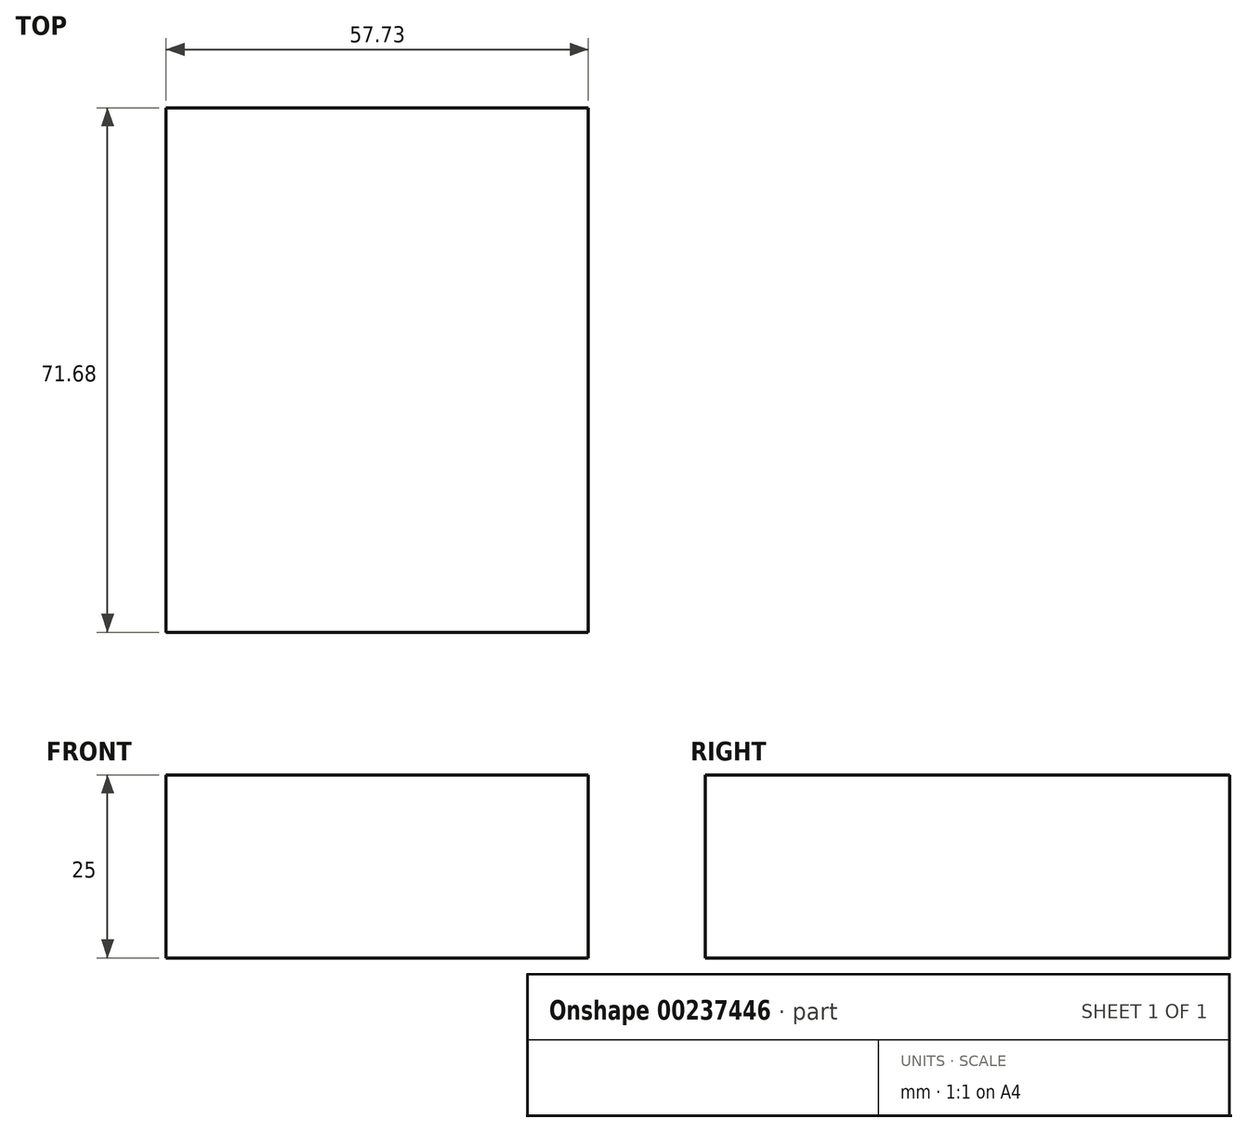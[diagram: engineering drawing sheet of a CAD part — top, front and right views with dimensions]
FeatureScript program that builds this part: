
annotation { "Feature Type Name" : "Feature", "Feature Type Description" : "" }
export const myFeature = defineFeature(function(context is Context, id is Id, definition is map)
    precondition{}
    {
        {
            var Q0;
            Q0=qCreatedBy(makeId("Top.planeOp"),FACE);
            var sketch = newSketch(context, id + "F0", { "sketchPlane" : qUnion([Q0])});
            skLineSegment(sketch, "E0.bottom", {"start": v(-76.87, -35.84) * mm, "end": v(-134.6, -35.84) * mm});
            skLineSegment(sketch, "E0.top", {"start": v(-76.87, 35.84) * mm, "end": v(-134.6, 35.84) * mm});
            skLineSegment(sketch, "E0.left", {"start": v(-76.87, -35.84) * mm, "end": v(-76.87, 35.84) * mm});
            skLineSegment(sketch, "E0.right", {"start": v(-134.6, -35.84) * mm, "end": v(-134.6, 35.84) * mm});
            skPoint(sketch, "E0.middle", {"position": v(-105.73, 0) * mm});
            skSolve(sketch);
        }
        {
            var Q0;
            Q0=makeQuery(id+"F0.imprint","IMPRINT",FACE,{"disambiguationData":[TD([[makeQuery(id+"F0.imprint","IMPRINT",EDGE,{"derivedFrom":sQuery(id+"F0.wireOp",EDGE,"E0.bottom")}),-1.0]])]});
            extrude(context, id + "F1", {"entities" : qUnion([Q0]), "depth" : 25 * mm});
        }
    });
